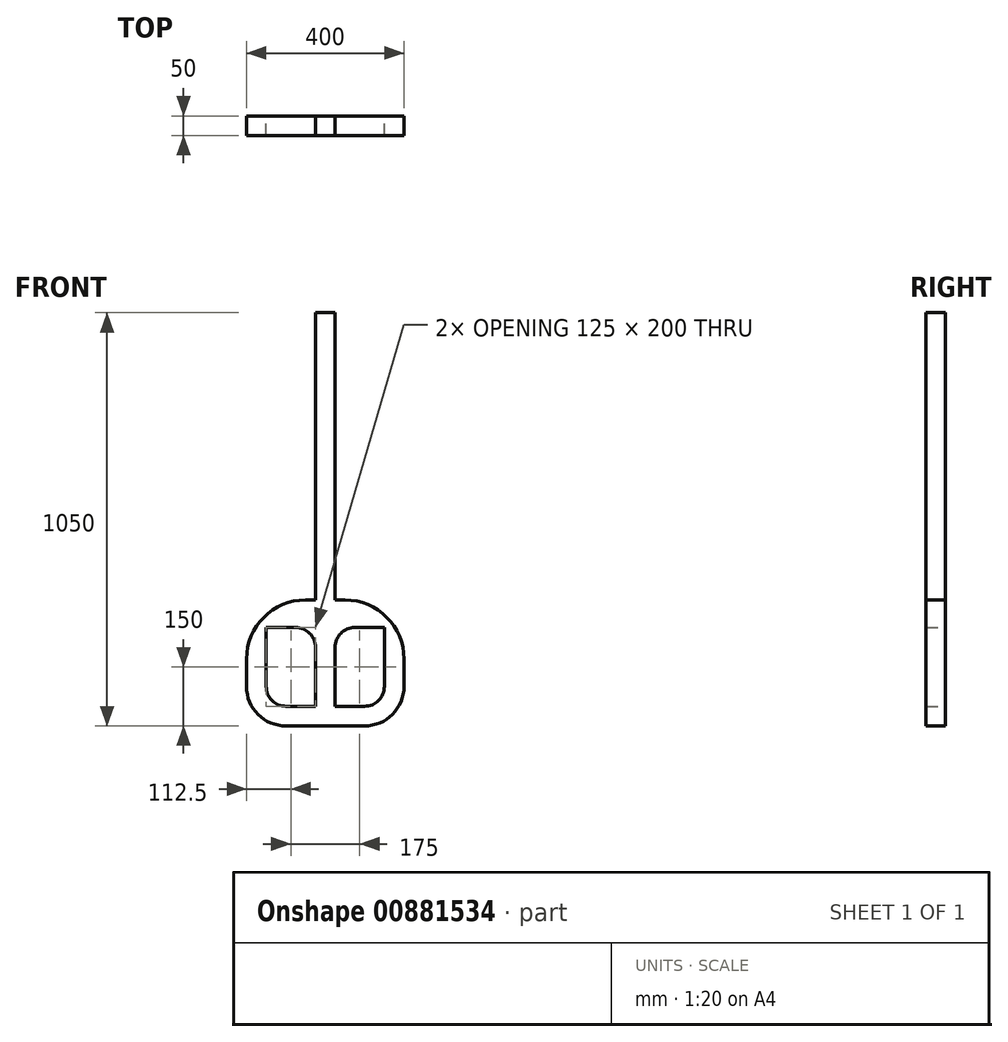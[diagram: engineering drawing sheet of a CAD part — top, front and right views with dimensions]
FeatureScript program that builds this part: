
annotation { "Feature Type Name" : "Feature", "Feature Type Description" : "" }
export const myFeature = defineFeature(function(context is Context, id is Id, definition is map)
    precondition{}
    {
        {
            var Q0;
            Q0=qCreatedBy(makeId("Top.planeOp"),FACE);
            var sketch = newSketch(context, id + "F0", { "sketchPlane" : qUnion([Q0])});
            skLineSegment(sketch, "E0.bottom", {"start": v(-25, -25) * mm, "end": v(25, -25) * mm});
            skLineSegment(sketch, "E0.top", {"start": v(-25, 25) * mm, "end": v(25, 25) * mm});
            skLineSegment(sketch, "E0.left", {"start": v(-25, -25) * mm, "end": v(-25, 25) * mm});
            skLineSegment(sketch, "E0.right", {"start": v(25, -25) * mm, "end": v(25, 25) * mm});
            skPoint(sketch, "E0.middle", {"position": v(0, 0) * mm});
            skLineSegment(sketch, "E1", {"start": v(0, 0) * mm, "end": v(-150, 0) * mm});
            skPoint(sketch, "E1.endSnap0", {"position": v(-25, 0) * mm});
            skLineSegment(sketch, "E2", {"start": v(0, 0) * mm, "end": v(150, 0) * mm, "construction": true});
            skLineSegment(sketch, "E3", {"start": v(-150, 0) * mm, "end": v(-200, 0) * mm});
            skLineSegment(sketch, "E4", {"start": v(150, 0) * mm, "end": v(200, 0) * mm});
            skSolve(sketch);
        }
        {
            var Q0;
            {var subQ0=sQuery(id+"F0.wireOp",EDGE,"E0.bottom");Q0=makeQuery(id+"F0.imprint","IMPRINT",FACE,{"disambiguationData":[TD([[makeQuery(id+"F0.imprint","IMPRINT",EDGE,{"derivedFrom":subQ0}),1.0]])]});}
            extrude(context, id + "F1", {"entities" : qUnion([Q0]), "depth" : 1000 * mm, "offsetDistance" : 25 * mm});
        }
        {
            var Q0;
            Q0=qCreatedBy(makeId("Front.planeOp"),FACE);
            var sketch = newSketch(context, id + "F2", { "sketchPlane" : qUnion([Q0])});
            skLineSegment(sketch, "E5.bottom", {"start": v(0, 0) * mm, "end": v(-200, 0) * mm});
            skLineSegment(sketch, "E5.top", {"start": v(0, -50) * mm, "end": v(-200, -50) * mm});
            skLineSegment(sketch, "E5.left", {"start": v(0, 0) * mm, "end": v(0, -50) * mm});
            skLineSegment(sketch, "E5.right", {"start": v(-200, 0) * mm, "end": v(-200, -50) * mm});
            skLineSegment(sketch, "E6.bottom", {"start": v(0, 0) * mm, "end": v(200, 0) * mm});
            skLineSegment(sketch, "E6.top", {"start": v(0, -50) * mm, "end": v(200, -50) * mm});
            skLineSegment(sketch, "E6.right", {"start": v(200, 0) * mm, "end": v(200, -50) * mm});
            skLineSegment(sketch, "E7.bottom", {"start": v(-200, 0) * mm, "end": v(-150, 0) * mm});
            skLineSegment(sketch, "E7.top", {"start": v(-200, 200) * mm, "end": v(-150, 200) * mm});
            skLineSegment(sketch, "E7.left", {"start": v(-200, 0) * mm, "end": v(-200, 200) * mm});
            skLineSegment(sketch, "E7.right", {"start": v(-150, 0) * mm, "end": v(-150, 200) * mm});
            skLineSegment(sketch, "E8.bottom", {"start": v(200, 0) * mm, "end": v(150, 0) * mm});
            skLineSegment(sketch, "E8.top", {"start": v(200, 200) * mm, "end": v(150, 200) * mm});
            skLineSegment(sketch, "E8.left", {"start": v(200, 0) * mm, "end": v(200, 200) * mm});
            skLineSegment(sketch, "E8.right", {"start": v(150, 0) * mm, "end": v(150, 200) * mm});
            skSolve(sketch);
        }
        {
            var Q0;
            Q0 = qSketchRegion(id + "F2", true);
            extrude(context, id + "F3", {"entities" : qUnion([Q0]), "operationType" : NewBodyOperationType.ADD, "depth" : 25 * mm, "offsetDistance" : 25 * mm, "hasSecondDirection" : true, "secondDirectionOppositeDirection" : true, "secondDirectionDepth" : 25 * mm});
        }
        {
            var Q0;
            Q0=qCreatedBy(makeId("Front.planeOp"),FACE);
            var sketch = newSketch(context, id + "F4", { "sketchPlane" : qUnion([Q0])});
            skLineSegment(sketch, "E9", {"start": v(0, 0) * mm, "end": v(-200, 0) * mm});
            skLineSegment(sketch, "E10", {"start": v(-200, 0) * mm, "end": v(-200, 200) * mm});
            skLineSegment(sketch, "E11", {"start": v(-25, 0) * mm, "end": v(-150, 0) * mm, "construction": true});
            skLineSegment(sketch, "E12", {"start": v(0, 0) * mm, "end": v(150, 0) * mm});
            skLineSegment(sketch, "E13", {"start": v(150, 0) * mm, "end": v(150, 170) * mm, "construction": true});
            skLineSegment(sketch, "E14", {"start": v(-200, 0) * mm, "end": v(-200, 170) * mm, "construction": true});
            skLineSegment(sketch, "E15", {"start": v(200, 0) * mm, "end": v(200, 200) * mm, "construction": true});
            skLineSegment(sketch, "E16.right", {"start": v(25, 140) * mm, "end": v(25, 270) * mm});
            skLineSegment(sketch, "E17.trimOffspring", {"start": v(-25, 220) * mm, "end": v(-25, 270) * mm, "construction": true});
            skLineSegment(sketch, "E18.bottom", {"start": v(-25, 270) * mm, "end": v(-200, 270) * mm});
            skLineSegment(sketch, "E18.top", {"start": v(-25, 200) * mm, "end": v(-200, 200) * mm});
            skLineSegment(sketch, "E18.left", {"start": v(-25, 270) * mm, "end": v(-25, 200) * mm});
            skLineSegment(sketch, "E18.right", {"start": v(-200, 270) * mm, "end": v(-200, 200) * mm});
            skLineSegment(sketch, "E19.bottom", {"start": v(25, 270) * mm, "end": v(200, 270) * mm});
            skLineSegment(sketch, "E19.top", {"start": v(25, 200) * mm, "end": v(200, 200) * mm});
            skLineSegment(sketch, "E19.left", {"start": v(25, 270) * mm, "end": v(25, 200) * mm});
            skLineSegment(sketch, "E19.right", {"start": v(200, 270) * mm, "end": v(200, 200) * mm});
            skSolve(sketch);
        }
        {
            var Q0;
            Q0 = qSketchRegion(id + "F4", true);
            extrude(context, id + "F5", {"entities" : qUnion([Q0]), "operationType" : NewBodyOperationType.ADD, "depth" : 25 * mm, "offsetDistance" : 25 * mm, "hasSecondDirection" : true, "secondDirectionOppositeDirection" : true, "secondDirectionDepth" : 25 * mm});
        }
        {
            var Q0;
            Q0=makeQuery(id+"F5.opExtrude","SWEPT_EDGE",EDGE,{"disambiguationData":[OSD([sQuery(id+"F4.wireOp",EDGE,"E19.bottom"),sQuery(id+"F4.wireOp",EDGE,"E19.right")])]});
            var Q1;
            Q1=makeQuery(id+"F5.opExtrude","SWEPT_EDGE",EDGE,{"disambiguationData":[OSD([sQuery(id+"F4.wireOp",EDGE,"E18.bottom"),sQuery(id+"F4.wireOp",EDGE,"E18.right")])]});
            fillet(context, id + "F6", {"entities" : qUnion([Q0, Q1]), "radius" : 150 * mm, "tangentPropagation" : true, "allowEdgeOverflow" : false});
        }
        {
            var Q0;
            Q0=makeQuery(id+"F3.opExtrude","SWEPT_EDGE",EDGE,{"disambiguationData":[OSD([sQuery(id+"F2.wireOp",EDGE,"E5.top"),sQuery(id+"F2.wireOp",EDGE,"E5.right")])]});
            var Q1;
            Q1=makeQuery(id+"F3.opExtrude","SWEPT_EDGE",EDGE,{"disambiguationData":[OSD([sQuery(id+"F2.wireOp",EDGE,"E6.top"),sQuery(id+"F2.wireOp",EDGE,"E6.right")])]});
            fillet(context, id + "F7", {"entities" : qUnion([Q0, Q1]), "radius" : 100 * mm, "tangentPropagation" : true, "allowEdgeOverflow" : false});
        }
        {
            var Q0;
            Q0=makeQuery(id+"F5.opExtrude","SWEPT_EDGE",EDGE,{"disambiguationData":[OSD([sQuery(id+"F4.wireOp",EDGE,"E18.top"),sQuery(id+"F4.wireOp",EDGE,"E18.left")])]});
            var Q1;
            Q1=makeQuery(id+"F5.opExtrude","SWEPT_EDGE",EDGE,{"disambiguationData":[OSD([sQuery(id+"F4.wireOp",EDGE,"E19.top"),sQuery(id+"F4.wireOp",EDGE,"E19.left")])]});
            var Q2;
            Q2=makeQuery(id+"F3.opExtrude","SWEPT_EDGE",EDGE,{"disambiguationData":[OSD([sQuery(id+"F2.wireOp",EDGE,"E7.top"),sQuery(id+"F2.wireOp",EDGE,"E7.right")])]});
            var Q3;
            Q3=makeQuery(id+"F3.opExtrude","SWEPT_EDGE",EDGE,{"disambiguationData":[OSD([sQuery(id+"F2.wireOp",EDGE,"E8.top"),sQuery(id+"F2.wireOp",EDGE,"E8.right")])]});
            var Q4;
            Q4=makeQuery(id+"F3.opExtrude","SWEPT_EDGE",EDGE,{"disambiguationData":[OSD([sQuery(id+"F2.wireOp",EDGE,"E5.bottom"),sQuery(id+"F2.wireOp",EDGE,"E7.bottom"),sQuery(id+"F2.wireOp",EDGE,"E7.right")])]});
            var Q5;
            Q5=makeQuery(id+"F3.opExtrude","SWEPT_EDGE",EDGE,{"disambiguationData":[OSD([sQuery(id+"F2.wireOp",EDGE,"E6.bottom"),sQuery(id+"F2.wireOp",EDGE,"E8.bottom"),sQuery(id+"F2.wireOp",EDGE,"E8.right")])]});
            fillet(context, id + "F8", {"entities" : qUnion([Q0, Q1, Q2, Q3, Q4, Q5]), "radius" : 50 * mm, "tangentPropagation" : true, "allowEdgeOverflow" : false});
        }
    });
